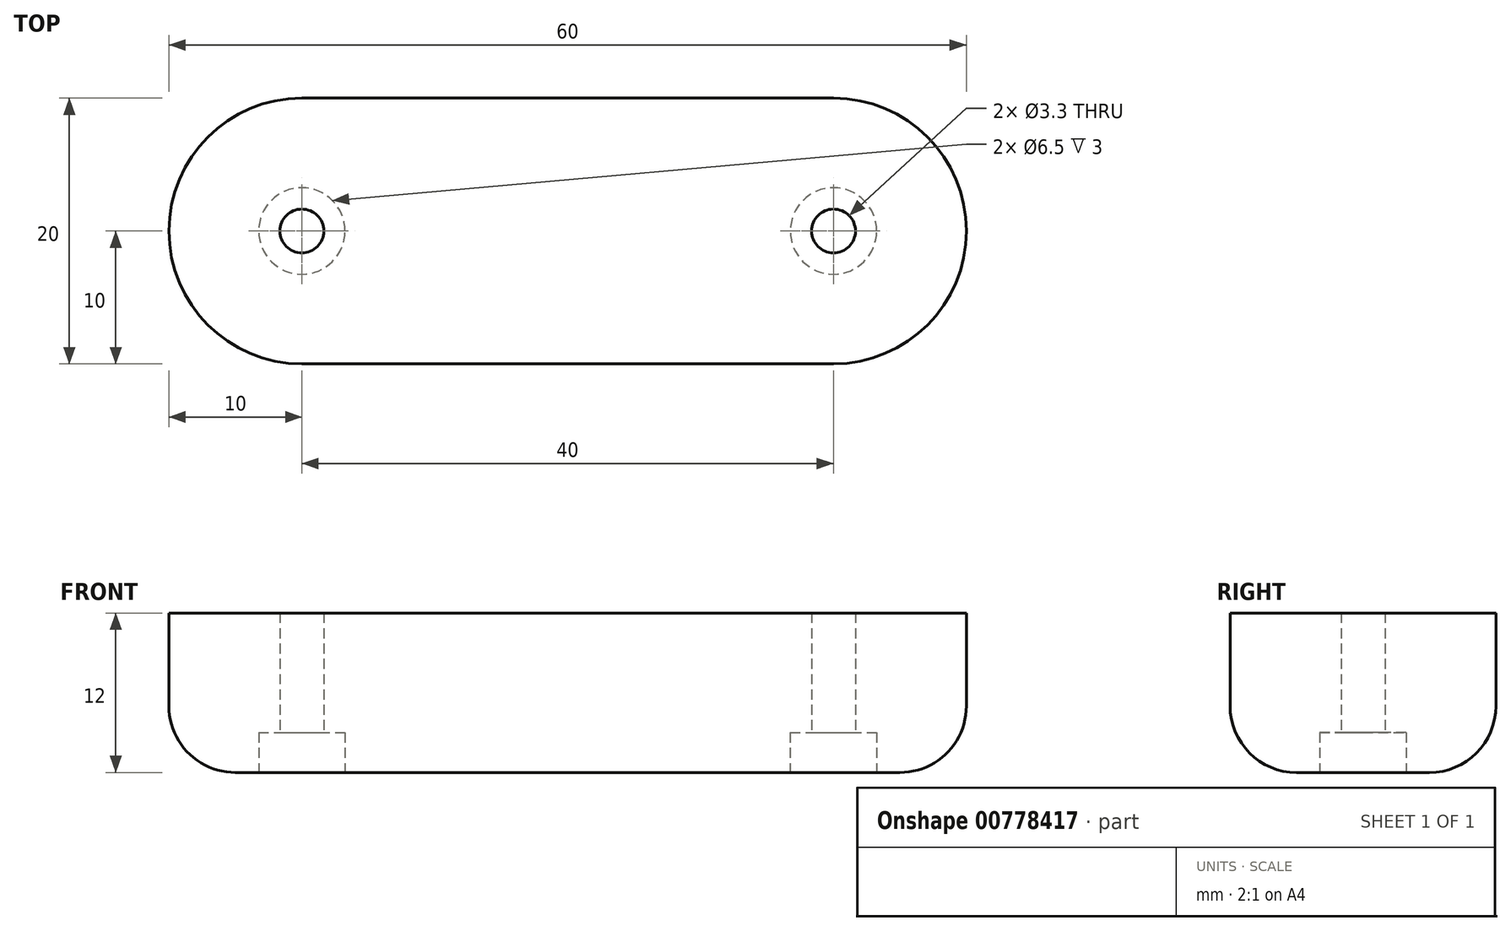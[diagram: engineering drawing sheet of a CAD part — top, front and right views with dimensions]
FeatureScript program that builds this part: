
annotation { "Feature Type Name" : "Feature", "Feature Type Description" : "" }
export const myFeature = defineFeature(function(context is Context, id is Id, definition is map)
    precondition{}
    {
        {
            var Q0;
            Q0=qCreatedBy(makeId("Top.planeOp"),FACE);
            var sketch = newSketch(context, id + "F0", { "sketchPlane" : qUnion([Q0])});
            skArc(sketch, "E0", {"start": v(0, 10) * mm, "mid": v(-10, 0) * mm, "end": v(0, -10) * mm});
            skArc(sketch, "E1", {"start": v(40, -10) * mm, "mid": v(50, 0) * mm, "end": v(40, 10) * mm});
            skLineSegment(sketch, "E2", {"start": v(0, 10) * mm, "end": v(40, 10) * mm});
            skLineSegment(sketch, "E3", {"start": v(0, -10) * mm, "end": v(40, -10) * mm});
            skPoint(sketch, "E4", {"position": v(-86.43, 17.68) * mm});
            skSolve(sketch);
        }
        {
            var Q0;
            Q0 = qSketchRegion(id + "F0", true);
            extrude(context, id + "F1", {"entities" : qUnion([Q0]), "depth" : 12 * mm, "offsetDistance" : 25 * mm});
        }
        {
            var Q0;
            Q0=sQuery(id+"F0.wireOp",VERTEX,"E1.center");
            var Q1;
            Q1=sQuery(id+"F0.wireOp",VERTEX,"E0.center");
            var Q2;
            Q2=makeQuery(id+"F1.opExtrude","SWEPT_BODY",BODY,{"disambiguationData":[OSD([sQuery(id+"F0.wireOp",EDGE,"E0"),sQuery(id+"F0.wireOp",EDGE,"E1"),sQuery(id+"F0.wireOp",EDGE,"E2"),sQuery(id+"F0.wireOp",EDGE,"E3")])]});
            hole(context, id + "F2", {"style" : HoleStyle.C_BORE, "endStyle" : HoleEndStyle.THROUGH, "oppositeDirection" : true, "standardTappedOrClearance" : lookupTablePath({ "standard" : "ISO", "fit" : "Normal", "size" : "M3", "type" : "Clearance" }), "standardBlindInLast" : lookupTablePath({ "fit" : "Standard", "standard" : "ISO", "size" : "M3", "type" : "Clearance" }), "holeDiameter" : 3.3 * mm, "cBoreDiameter" : 6.5 * mm, "cBoreDepth" : 3 * mm, "majorDiameter" : 5 * mm, "isTappedThrough" : true, "tappedDepth" : 12 * mm, "tapClearance" : 3, "locations" : qUnion([Q0, Q1]), "scope" : qUnion([Q2])});
        }
        {
            var Q0;
            Q0=makeQuery(id+"F1.opExtrude","CAP_EDGE",EDGE,{"disambiguationData":[OSD([sQuery(id+"F0.wireOp",EDGE,"E3")])],"isStart":true});
            fillet(context, id + "F3", {"entities" : qUnion([Q0]), "radius" : 5 * mm, "tangentPropagation" : true, "allowEdgeOverflow" : false});
        }
    });
